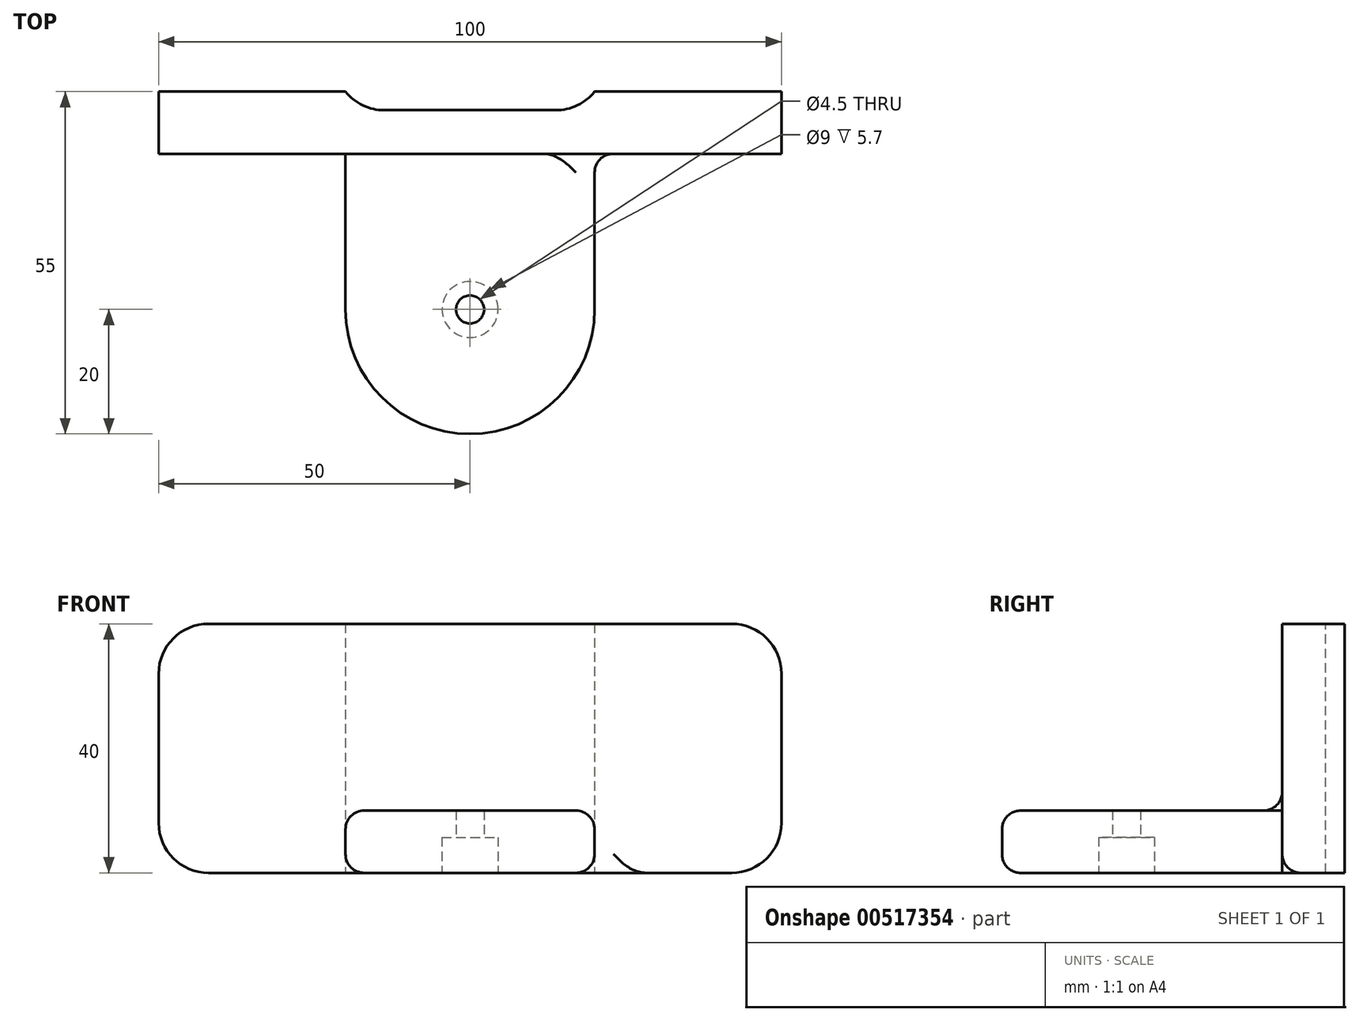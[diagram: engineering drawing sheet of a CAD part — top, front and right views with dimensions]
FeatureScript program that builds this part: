
annotation { "Feature Type Name" : "Feature", "Feature Type Description" : "" }
export const myFeature = defineFeature(function(context is Context, id is Id, definition is map)
    precondition{}
    {
        {
            var Q0;
            Q0=qCreatedBy(makeId("Front.planeOp"),FACE);
            var sketch = newSketch(context, id + "F0", { "sketchPlane" : qUnion([Q0])});
            skLineSegment(sketch, "E0.bottom", {"start": v(0, 0) * mm, "end": v(100, 0) * mm});
            skLineSegment(sketch, "E0.top", {"start": v(0, 40) * mm, "end": v(100, 40) * mm});
            skLineSegment(sketch, "E0.left", {"start": v(0, 0) * mm, "end": v(0, 40) * mm});
            skLineSegment(sketch, "E0.right", {"start": v(100, 0) * mm, "end": v(100, 40) * mm});
            skSolve(sketch);
        }
        {
            var Q0;
            Q0 = qSketchRegion(id + "F0", true);
            extrude(context, id + "F1", {"entities" : qUnion([Q0]), "depth" : 10 * mm, "offsetDistance" : 25 * mm});
        }
        {
            var Q0;
            Q0=qCreatedBy(makeId("Top.planeOp"),FACE);
            var sketch = newSketch(context, id + "F2", { "sketchPlane" : qUnion([Q0])});
            skLineSegment(sketch, "E1", {"start": v(30, 0) * mm, "end": v(30, -35) * mm});
            skArc(sketch, "E2", {"start": v(30, -35) * mm, "mid": v(50, -55) * mm, "end": v(70, -35) * mm});
            skLineSegment(sketch, "E3", {"start": v(70, -35) * mm, "end": v(70, 0) * mm});
            skLineSegment(sketch, "E4", {"start": v(30, 0) * mm, "end": v(70, 0) * mm});
            skSolve(sketch);
        }
        {
            var Q0;
            Q0 = qSketchRegion(id + "F2", true);
            extrude(context, id + "F3", {"entities" : qUnion([Q0]), "operationType" : NewBodyOperationType.ADD, "depth" : 10 * mm, "offsetDistance" : 25 * mm});
        }
        {
            var Q0;
            Q0=makeQuery(id+"F3.boolean.opBoolean","MERGE",FACE,{"derivedFrom":[makeQuery(id+"F1.opExtrude","SWEPT_FACE",FACE,{"disambiguationData":[OSD([sQuery(id+"F0.wireOp",EDGE,"E0.bottom")])]}),makeQuery(id+"F3.opExtrude","CAP_FACE",FACE,{"disambiguationData":[OSD([sQuery(id+"F2.wireOp",EDGE,"E1"),sQuery(id+"F2.wireOp",EDGE,"E2"),sQuery(id+"F2.wireOp",EDGE,"E3"),sQuery(id+"F2.wireOp",EDGE,"E4")])],"isStart":true})]});
            var sketch = newSketch(context, id + "F4", { "sketchPlane" : qUnion([Q0])});
            skLineSegment(sketch, "E5.bottom", {"start": v(30, 0) * mm, "end": v(70, 0) * mm});
            skLineSegment(sketch, "E5.top", {"start": v(30, 3) * mm, "end": v(70, 3) * mm});
            skLineSegment(sketch, "E5.left", {"start": v(30, 0) * mm, "end": v(30, 3) * mm});
            skLineSegment(sketch, "E5.right", {"start": v(70, 0) * mm, "end": v(70, 3) * mm});
            skSolve(sketch);
        }
        {
            var Q0;
            Q0 = qSketchRegion(id + "F4", true);
            extrude(context, id + "F5", {"entities" : qUnion([Q0]), "operationType" : NewBodyOperationType.REMOVE, "endBound" : BoundingType.THROUGH_ALL, "oppositeDirection" : true, "depth" : 25 * mm, "offsetDistance" : 25 * mm});
        }
        {
            var Q0;
            Q0=makeQuery(id+"F3.boolean.opBoolean","MERGE",FACE,{"derivedFrom":[makeQuery(id+"F1.opExtrude","SWEPT_FACE",FACE,{"disambiguationData":[OSD([sQuery(id+"F0.wireOp",EDGE,"E0.bottom")])]}),makeQuery(id+"F3.opExtrude","CAP_FACE",FACE,{"disambiguationData":[OSD([sQuery(id+"F2.wireOp",EDGE,"E1"),sQuery(id+"F2.wireOp",EDGE,"E2"),sQuery(id+"F2.wireOp",EDGE,"E3"),sQuery(id+"F2.wireOp",EDGE,"E4")])],"isStart":true})]});
            var sketch = newSketch(context, id + "F6", { "sketchPlane" : qUnion([Q0])});
            skCircle(sketch, "E6", {"center": v(50, 35) * mm, "radius": 2.25 * mm});
            skSolve(sketch);
        }
        {
            var Q0;
            Q0 = qSketchRegion(id + "F6", true);
            extrude(context, id + "F7", {"entities" : qUnion([Q0]), "operationType" : NewBodyOperationType.REMOVE, "endBound" : BoundingType.THROUGH_ALL, "oppositeDirection" : true, "depth" : 25 * mm, "offsetDistance" : 25 * mm});
        }
        {
            var Q0;
            Q0=makeQuery(id+"F3.boolean.opBoolean","MERGE",FACE,{"derivedFrom":[makeQuery(id+"F1.opExtrude","SWEPT_FACE",FACE,{"disambiguationData":[OSD([sQuery(id+"F0.wireOp",EDGE,"E0.bottom")])]}),makeQuery(id+"F3.opExtrude","CAP_FACE",FACE,{"disambiguationData":[OSD([sQuery(id+"F2.wireOp",EDGE,"E1"),sQuery(id+"F2.wireOp",EDGE,"E2"),sQuery(id+"F2.wireOp",EDGE,"E3"),sQuery(id+"F2.wireOp",EDGE,"E4")])],"isStart":true})]});
            var sketch = newSketch(context, id + "F8", { "sketchPlane" : qUnion([Q0])});
            skCircle(sketch, "E7", {"center": v(50, 35) * mm, "radius": 4.5 * mm});
            skSolve(sketch);
        }
        {
            var Q0;
            Q0 = qSketchRegion(id + "F8", true);
            extrude(context, id + "F9", {"entities" : qUnion([Q0]), "operationType" : NewBodyOperationType.REMOVE, "oppositeDirection" : true, "depth" : 5.7 * mm, "offsetDistance" : 25 * mm});
        }
        {
            var Q0;
            Q0=makeQuery(id+"F1.opExtrude","SWEPT_EDGE",EDGE,{"disambiguationData":[OSD([sQuery(id+"F0.wireOp",EDGE,"E0.bottom"),sQuery(id+"F0.wireOp",EDGE,"E0.right")])]});
            var Q1;
            Q1=makeQuery(id+"F1.opExtrude","SWEPT_EDGE",EDGE,{"disambiguationData":[OSD([sQuery(id+"F0.wireOp",EDGE,"E0.top"),sQuery(id+"F0.wireOp",EDGE,"E0.right")])]});
            var Q2;
            Q2=makeQuery(id+"F1.opExtrude","SWEPT_EDGE",EDGE,{"disambiguationData":[OSD([sQuery(id+"F0.wireOp",EDGE,"E0.bottom"),sQuery(id+"F0.wireOp",EDGE,"E0.left")])]});
            var Q3;
            Q3=makeQuery(id+"F1.opExtrude","SWEPT_EDGE",EDGE,{"disambiguationData":[OSD([sQuery(id+"F0.wireOp",EDGE,"E0.top"),sQuery(id+"F0.wireOp",EDGE,"E0.left")])]});
            var Q4;
            Q4=makeQuery(id+"F5.boolean.opBoolean","COPY",EDGE,{"derivedFrom":makeQuery(id+"F5.opExtrude","SWEPT_EDGE",EDGE,{"disambiguationData":[OSD([sQuery(id+"F4.wireOp",EDGE,"E5.top"),sQuery(id+"F4.wireOp",EDGE,"E5.right")])]})});
            var Q5;
            Q5=makeQuery(id+"F5.boolean.opBoolean","COPY",EDGE,{"derivedFrom":makeQuery(id+"F5.opExtrude","SWEPT_EDGE",EDGE,{"disambiguationData":[OSD([sQuery(id+"F4.wireOp",EDGE,"E5.top"),sQuery(id+"F4.wireOp",EDGE,"E5.left")])]})});
            fillet(context, id + "F10", {"entities" : qUnion([Q0, Q1, Q2, Q3, Q4, Q5]), "radius" : 8 * mm, "tangentPropagation" : true, "allowEdgeOverflow" : false});
        }
        {
            var Q0;
            Q0=makeQuery(id+"F3.opExtrude","CAP_EDGE",EDGE,{"disambiguationData":[OSD([sQuery(id+"F2.wireOp",EDGE,"E2")])],"isStart":false});
            var Q1;
            Q1=makeQuery(id+"F3.opExtrude","CAP_EDGE",EDGE,{"disambiguationData":[OSD([sQuery(id+"F2.wireOp",EDGE,"E2")])],"isStart":true});
            var Q2;
            Q2=makeQuery(id+"F3.boolean.opBoolean","INTERSECT",EDGE,{"derivedFrom":[makeQuery(id+"F1.opExtrude","CAP_FACE",FACE,{"disambiguationData":[OSD([sQuery(id+"F0.wireOp",EDGE,"E0.bottom"),sQuery(id+"F0.wireOp",EDGE,"E0.top"),sQuery(id+"F0.wireOp",EDGE,"E0.left"),sQuery(id+"F0.wireOp",EDGE,"E0.right")])],"isStart":false}),makeQuery(id+"F3.opExtrude","SWEPT_FACE",FACE,{"disambiguationData":[OSD([sQuery(id+"F2.wireOp",EDGE,"E3")])]})]});
            fillet(context, id + "F11", {"entities" : qUnion([Q0, Q1, Q2]), "radius" : 3 * mm, "tangentPropagation" : true, "allowEdgeOverflow" : false});
        }
    });
